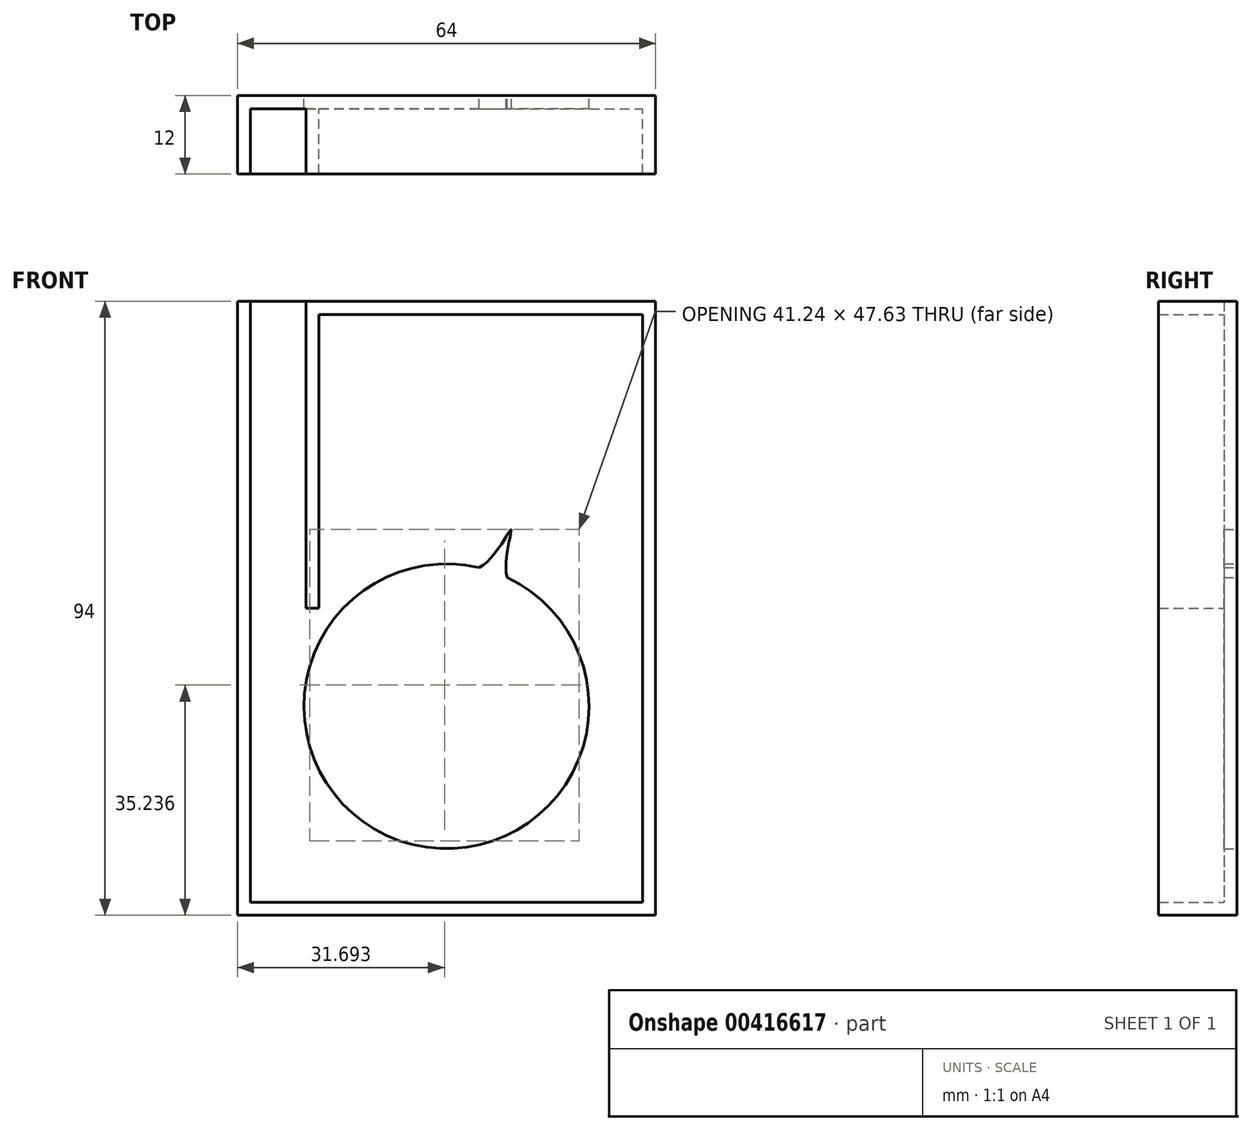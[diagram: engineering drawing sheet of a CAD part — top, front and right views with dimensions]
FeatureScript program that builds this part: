
annotation { "Feature Type Name" : "Feature", "Feature Type Description" : "" }
export const myFeature = defineFeature(function(context is Context, id is Id, definition is map)
    precondition{}
    {
        {
            var Q0;
            Q0=qCreatedBy(makeId("Front.planeOp"),FACE);
            var sketch = newSketch(context, id + "F0", { "sketchPlane" : qUnion([Q0])});
            skLineSegment(sketch, "E0.bottom", {"start": v(-51.5, 92) * mm, "end": v(-2, 92) * mm});
            skLineSegment(sketch, "E0.top", {"start": v(-62, 2) * mm, "end": v(-2, 2) * mm});
            skLineSegment(sketch, "E0.left", {"start": v(-62, 92) * mm, "end": v(-62, 2) * mm});
            skLineSegment(sketch, "E0.right", {"start": v(-2, 92) * mm, "end": v(-2, 2) * mm});
            skLineSegment(sketch, "E1.0", {"start": v(-64, 94) * mm, "end": v(-62, 94) * mm});
            skLineSegment(sketch, "E1.1", {"start": v(-64, 94) * mm, "end": v(-64, 0) * mm});
            skLineSegment(sketch, "E1.2", {"start": v(-64, 0) * mm, "end": v(0, 0) * mm});
            skLineSegment(sketch, "E1.3", {"start": v(0, 94) * mm, "end": v(0, 0) * mm});
            skPoint(sketch, "E2", {"position": v(-53.5, 94) * mm});
            skPoint(sketch, "E3", {"position": v(-62, 92) * mm});
            skPoint(sketch, "E4", {"position": v(-62, 94) * mm});
            skLineSegment(sketch, "E5", {"start": v(-53.5, 92) * mm, "end": v(-53.5, 94) * mm});
            skLineSegment(sketch, "E6", {"start": v(-62, 92) * mm, "end": v(-62, 94) * mm});
            skLineSegment(sketch, "E7.trimOffspring", {"start": v(-53.5, 94) * mm, "end": v(0, 94) * mm});
            skLineSegment(sketch, "E8", {"start": v(-62, 94) * mm, "end": v(-53.5, 94) * mm});
            skLineSegment(sketch, "E9", {"start": v(-53.5, 92) * mm, "end": v(-53.5, 47) * mm});
            skLineSegment(sketch, "E10.0", {"start": v(-51.5, 92) * mm, "end": v(-51.5, 47) * mm});
            skLineSegment(sketch, "E11", {"start": v(-53.5, 47) * mm, "end": v(-51.5, 47) * mm});
            skCircle(sketch, "E12", {"center": v(-32, 32) * mm, "radius": 21.8 * mm});
            skFitSpline(sketch, "E13", {"points": [v(-27, 53.22) * mm, v(-22.11, 59.05) * mm, v(-22.7, 51.72) * mm], "startDerivative": vector(14.94, 7.84) * mm, "endDerivative": vector(4.62, -14.91) * mm});
            skSolve(sketch);
        }
        {
            var Q0;
            Q0=makeQuery(id+"F0.imprint","IMPRINT",FACE,{"disambiguationData":[TD([[makeQuery(id+"F0.imprint","IMPRINT",EDGE,{"derivedFrom":sQuery(id+"F0.wireOp",EDGE,"E0.bottom")}),-1.0]])]});
            extrude(context, id + "F1", {"entities" : qUnion([Q0]), "depth" : 2 * mm});
        }
        {
            var Q0;
            Q0=makeQuery(id+"F0.imprint","IMPRINT",FACE,{"disambiguationData":[TD([[makeQuery(id+"F0.imprint","IMPRINT",EDGE,{"derivedFrom":sQuery(id+"F0.wireOp",EDGE,"E0.bottom")}),1.0]])]});
            extrude(context, id + "F2", {"entities" : qUnion([Q0]), "operationType" : NewBodyOperationType.ADD, "depth" : 12 * mm});
        }
    });
